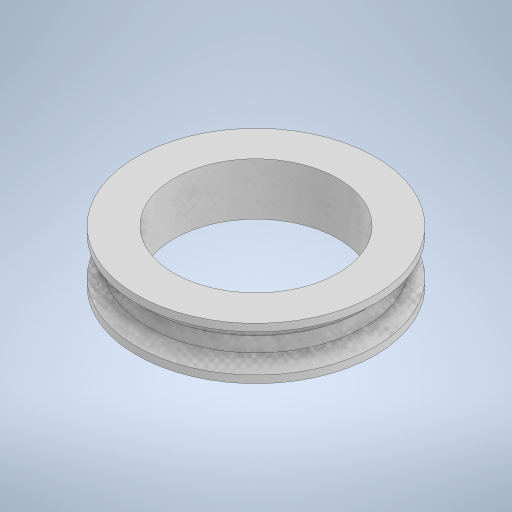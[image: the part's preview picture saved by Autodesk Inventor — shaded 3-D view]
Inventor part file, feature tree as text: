
AUTODESK INVENTOR PART (.ipt)
format: ipt  version: 2024 (Build 280153000, 153)  size: 419,328 bytes
history: native  units: mm
features: other x1, revolve x1, sketch x1
ambient origin geometry x8: Origin, YZ Plane, XZ Plane, XY Plane, X Axis, Y Axis, Z Axis, Center Point
bodies: Body1 (feature_tree)
feature tree (3):
  other  "Sólido1"
  revolve  "Revolución1"  [1 undecoded]
  sketch  "Boceto1"  dims[d2=5.0mm d3=1.0mm d4=135.0deg d5=1.5mm d6=7.0mm d7=11.0mm d8=90.0deg]
note: 1 required parameter value undecoded (feature->parameter linkage not recoverable at this tier; creation-order binding heuristic only, values carry confidence <= 0.55)
